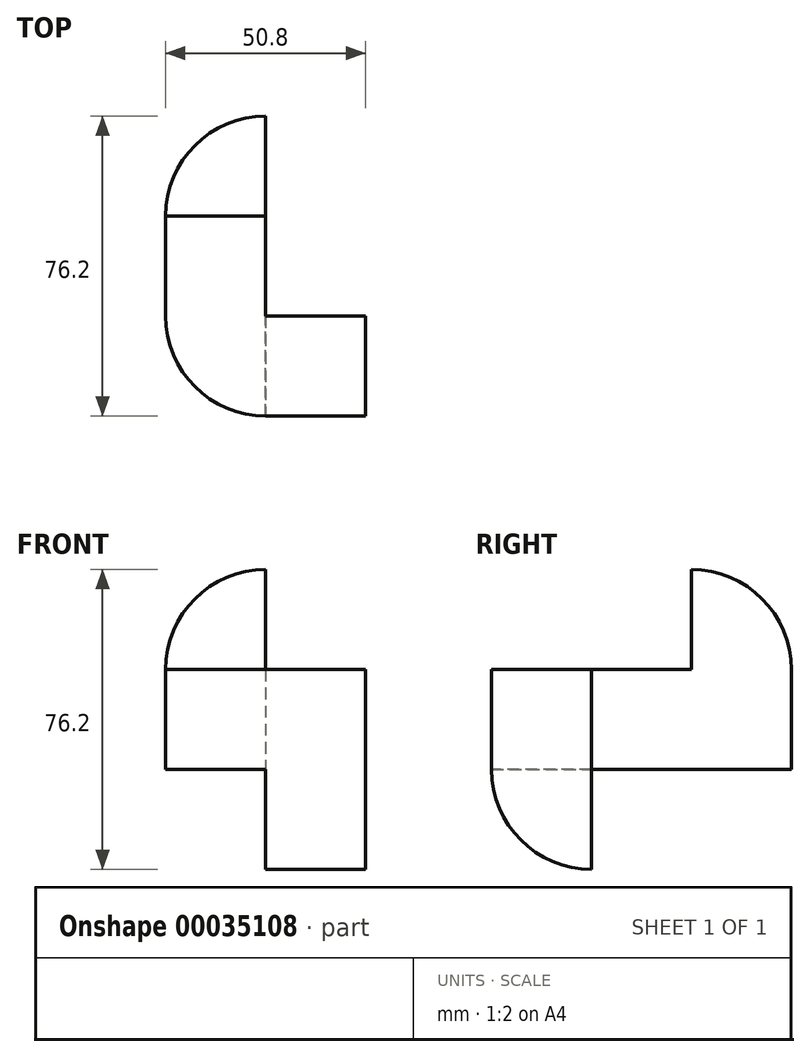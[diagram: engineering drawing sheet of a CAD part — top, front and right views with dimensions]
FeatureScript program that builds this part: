
annotation { "Feature Type Name" : "Feature", "Feature Type Description" : "" }
export const myFeature = defineFeature(function(context is Context, id is Id, definition is map)
    precondition{}
    {
        {
            var Q0;
            Q0=qCreatedBy(makeId("Top.planeOp"),FACE);
            var sketch = newSketch(context, id + "F0", { "sketchPlane" : qUnion([Q0])});
            skLineSegment(sketch, "E0", {"start": v(0, 0) * mm, "end": v(0, 25.4) * mm});
            skLineSegment(sketch, "E1", {"start": v(0, 25.4) * mm, "end": v(25.4, 25.4) * mm});
            skLineSegment(sketch, "E2", {"start": v(25.4, 25.4) * mm, "end": v(25.4, 0) * mm});
            skLineSegment(sketch, "E3", {"start": v(0, 0) * mm, "end": v(25.4, 0) * mm});
            skSolve(sketch);
        }
        {
            var Q0;
            Q0=makeQuery(id+"F0.imprint","IMPRINT",FACE,{"disambiguationData":[TD([[makeQuery(id+"F0.imprint","IMPRINT",EDGE,{"derivedFrom":sQuery(id+"F0.wireOp",EDGE,"E0")}),-1.0]])]});
            extrude(context, id + "F1", {"entities" : qUnion([Q0]), "depth" : 25.4 * mm});
        }
        {
            var Q0;
            Q0=makeQuery(id+"F1.opExtrude","CAP_FACE",FACE,{"disambiguationData":[OSD([sQuery(id+"F0.wireOp",EDGE,"E0"),sQuery(id+"F0.wireOp",EDGE,"E1"),sQuery(id+"F0.wireOp",EDGE,"E2"),sQuery(id+"F0.wireOp",EDGE,"E3")])],"isStart":false});
            var sketch = newSketch(context, id + "F2", { "sketchPlane" : qUnion([Q0])});
            skLineSegment(sketch, "E4", {"start": v(25.4, 0) * mm, "end": v(25.4, 25.4) * mm});
            skLineSegment(sketch, "E5", {"start": v(25.4, 25.4) * mm, "end": v(0, 25.4) * mm});
            skLineSegment(sketch, "E6", {"start": v(0, 25.4) * mm, "end": v(0, 76.2) * mm});
            skLineSegment(sketch, "E7", {"start": v(0, 76.2) * mm, "end": v(-25.4, 76.2) * mm});
            skLineSegment(sketch, "E8", {"start": v(-25.4, 76.2) * mm, "end": v(-25.4, 0) * mm});
            skLineSegment(sketch, "E9", {"start": v(-25.4, 0) * mm, "end": v(0, 0) * mm});
            skLineSegment(sketch, "E10", {"start": v(0, 0) * mm, "end": v(25.4, 0) * mm});
            skSolve(sketch);
        }
        {
            var Q0;
            Q0=makeQuery(id+"F2.imprint","IMPRINT",FACE,{"disambiguationData":[TD([[makeQuery(id+"F2.imprint","IMPRINT",EDGE,{"derivedFrom":sQuery(id+"F2.wireOp",EDGE,"E6")}),1.0]])]});
            var Q1;
            Q1=makeQuery(id+"F2.imprint","IMPRINT",FACE,{"disambiguationData":[TD([[makeQuery(id+"F2.imprint","IMPRINT",EDGE,{"derivedFrom":sQuery(id+"F2.wireOp",EDGE,"E4")}),-1.0]])]});
            extrude(context, id + "F3", {"entities" : qUnion([Q0, Q1]), "operationType" : NewBodyOperationType.ADD, "depth" : 25.4 * mm});
        }
        {
            var Q0;
            Q0=makeQuery(id+"F3.opExtrude","CAP_FACE",FACE,{"disambiguationData":[OSD([sQuery(id+"F2.wireOp",EDGE,"E4"),sQuery(id+"F2.wireOp",EDGE,"E5"),sQuery(id+"F2.wireOp",EDGE,"E6"),sQuery(id+"F2.wireOp",EDGE,"E7"),sQuery(id+"F2.wireOp",EDGE,"E8"),sQuery(id+"F2.wireOp",EDGE,"E9"),sQuery(id+"F2.wireOp",EDGE,"E10")])],"isStart":false});
            var sketch = newSketch(context, id + "F4", { "sketchPlane" : qUnion([Q0])});
            skLineSegment(sketch, "E11", {"start": v(-25.4, 76.2) * mm, "end": v(0, 76.2) * mm});
            skLineSegment(sketch, "E12", {"start": v(0, 76.2) * mm, "end": v(0, 50.8) * mm});
            skLineSegment(sketch, "E13", {"start": v(0, 50.8) * mm, "end": v(-25.4, 50.8) * mm});
            skLineSegment(sketch, "E14", {"start": v(-25.4, 50.8) * mm, "end": v(-25.4, 76.2) * mm});
            skSolve(sketch);
        }
        {
            var Q0;
            Q0=makeQuery(id+"F4.imprint","IMPRINT",FACE,{"disambiguationData":[TD([[makeQuery(id+"F4.imprint","IMPRINT",EDGE,{"derivedFrom":sQuery(id+"F4.wireOp",EDGE,"E11")}),1.0]])]});
            extrude(context, id + "F5", {"entities" : qUnion([Q0]), "operationType" : NewBodyOperationType.ADD, "depth" : 25.4 * mm});
        }
        {
            var Q0;
            Q0=makeQuery(id+"F1.opExtrude","CAP_EDGE",EDGE,{"disambiguationData":[OSD([sQuery(id+"F0.wireOp",EDGE,"E3")])],"isStart":true});
            var Q1;
            Q1=makeQuery(id+"F3.opExtrude","SWEPT_EDGE",EDGE,{"disambiguationData":[OSD([sQuery(id+"F2.wireOp",EDGE,"E8"),sQuery(id+"F2.wireOp",EDGE,"E9")])]});
            var Q2;
            Q2=makeQuery(id+"F5.opExtrude","CAP_EDGE",EDGE,{"disambiguationData":[OSD([sQuery(id+"F4.wireOp",EDGE,"E14")])],"isStart":false});
            var Q3;
            Q3=makeQuery(id+"F5.opExtrude","CAP_EDGE",EDGE,{"disambiguationData":[OSD([sQuery(id+"F4.wireOp",EDGE,"E11")])],"isStart":false});
            var Q4;
            Q4=makeQuery(id+"F5.boolean.opBoolean","MERGE",EDGE,{"derivedFrom":[makeQuery(id+"F3.opExtrude","SWEPT_EDGE",EDGE,{"disambiguationData":[OSD([sQuery(id+"F2.wireOp",EDGE,"E7"),sQuery(id+"F2.wireOp",EDGE,"E8")])]}),makeQuery(id+"F5.opExtrude","SWEPT_EDGE",EDGE,{"disambiguationData":[OSD([sQuery(id+"F4.wireOp",EDGE,"E11"),sQuery(id+"F4.wireOp",EDGE,"E14")])]})]});
            fillet(context, id + "F6", {"entities" : qUnion([Q0, Q1, Q2, Q3, Q4]), "radius" : 25.4 * mm, "tangentPropagation" : true, "allowEdgeOverflow" : false});
        }
    });
